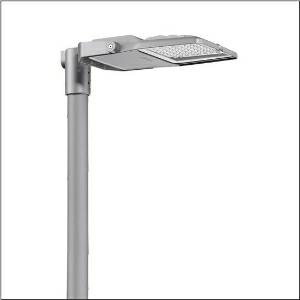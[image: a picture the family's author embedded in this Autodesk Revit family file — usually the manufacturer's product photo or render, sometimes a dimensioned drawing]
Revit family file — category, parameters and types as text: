
# Revit family: floodlight_fl_21_iq_mini___pl52_5xa7771b4d3a_0091
name_source: partatom
category: Lighting Fixtures
units: mm (PartAtom-declared; Revit-internal decimal feet)

## family parameters
Cut with Voids When Loaded = No
Host = Face
Light Source = No
Part Type = Normal
Room Calculation Point = No
Round Connector Dimension = Use Diameter
Shared = No

## types (1)
- --- (1 x LED, 6490 lm, 45.5 W, 4000K)
    Apparent Load = 46 VA
    CIE Flux Codes = 26 60 98 100 100
    Color Rendering = 70
    Color Temperature = 4000K
    Default Elevation = 1800 mm
    Description = Floodlight FL 21 iQ mini, floodlight, primary light control with lens, of PMMA, primary optical cover: protective disc, of toughened safety glass, transparent, light distribution: PL52, light emission: direct distribution, installation type: surface-mounted, LED, High Power LED, rated luminous flux: 6.490lm, luminous efficacy: 143lm/W, light colour: 740, colour temperature: 4000K, control gear: iQ Comfort/DALI, control: Auto-Match, Temp-Guard, Lumen-Switch, Night-Set, Smart-Wire, Light-Fading, Desk-Remote (wireless, voltage-free reading and setting of iQ features in the workshop via application-optimized NFC function/RFID function), optimised constant luminous flux control (CLO 2.0), with terminal, 6-pole, mains connection: 220..240V, AC, 50/60Hz, start of lifetime: 46W, end of service life: 48W, reduction: 22W, luminaire housing, of diecast aluminium, powder-coated, Siteco® metallic grey (DB 702S), corrosivity category C5 mid according to DIN EN ISO 12944, suitable for swimming pools, chlorine-resistant, sealing non-destructively replaceable, please order mast flange separately, mast bracket, of steel, galvanised, powder-coated, Siteco® metallic grey (DB 702S), protection rating (complete): IP66, insulation class (complete): insulation class II (safety insulation), certification: CE, ENEC, VDE, protection symbol: D, impact resistance: IK08, permissible operating ambient temperature: -40..+40°C, permissible operating ambient temperature for outdoor applications: -40..+50°C, standard: DIN EN 12944, LABS conformity tested according to VDMA 24364:2018-05, packaging unit: 1 piece

Light Distribution: PL52
    Height = 70 mm
    Lamp = 1 x LED
    Lamp Light Flux = 6490 lm
    Lamp Power = 45.5 W
    Lamp count = 1
    Length = 485 mm
    Luminous efficacy = 143 lm/W
    Manufacturer = Siteco
    ModVariant = No
    Model = 5XA7771B4D3A
    Number of Poles = 1
    OnlyDefault = Yes
    Power Factor = 1
    Product Name = Floodlight FL 21 iQ mini | PL52
    Product group = floodlight | pylon annexe
    ProductGroupID = 6200
    Protection Class = Protection class II
    Protection Degree = IP 66
    RLX_Detail_Level = 1
    RLX_Emergency_Light_Flux = 0 lm
    RLX_Emergency_Type = 0
    RLX_Emergency_Type_DB = No
    RlxData = <blob elided: 101401 chars, md5=430a8b75>
    Socket = socket
    Standby Power = 0 W
    System Light Flux = 6490 lm
    System Power = 46 W
    Type Comments = factory setting: luminous flux: 100 % | dim-lin: 254 | 463 mA
    Type Image = l_1007125.jpg
    URL = http://relux.com
    VarID = @adj_164988
    Voltage = 0 V
    Weight = 0.00 kg
    Width = 337 mm

## geometry (parser evidence)
native form markers: Blend x4, Sweep x12
no freeform markers — native parametric forms only
